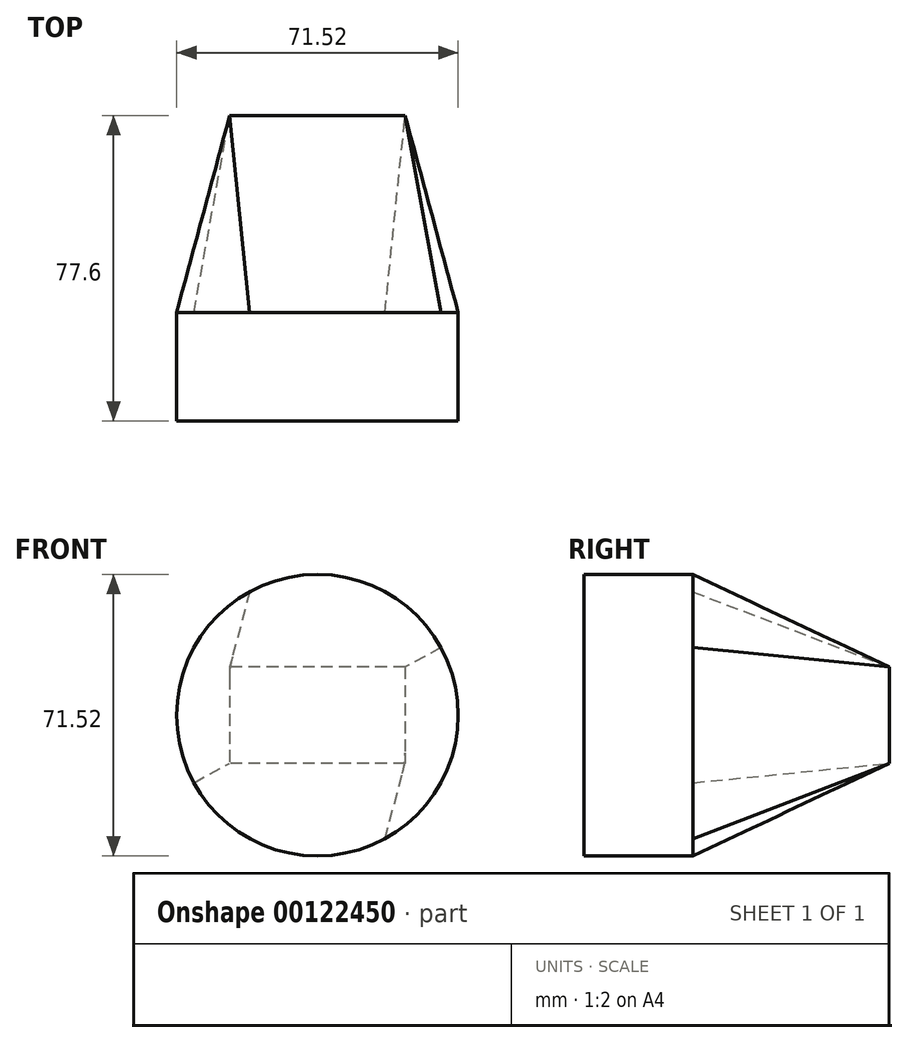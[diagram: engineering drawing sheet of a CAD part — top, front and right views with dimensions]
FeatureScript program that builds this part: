
annotation { "Feature Type Name" : "Feature", "Feature Type Description" : "" }
export const myFeature = defineFeature(function(context is Context, id is Id, definition is map)
    precondition{}
    {
        {
            var Q0;
            Q0=qCreatedBy(makeId("Front.planeOp"),FACE);
            var sketch = newSketch(context, id + "F0", { "sketchPlane" : qUnion([Q0])});
            skLineSegment(sketch, "E0.bottom", {"start": v(22.29, 12.2) * mm, "end": v(-22.29, 12.2) * mm});
            skLineSegment(sketch, "E0.top", {"start": v(22.29, -12.2) * mm, "end": v(-22.29, -12.2) * mm});
            skLineSegment(sketch, "E0.left", {"start": v(22.29, 12.2) * mm, "end": v(22.29, -12.2) * mm});
            skLineSegment(sketch, "E0.right", {"start": v(-22.29, 12.2) * mm, "end": v(-22.29, -12.2) * mm});
            skPoint(sketch, "E0.middle", {"position": v(0, 0) * mm});
            skSolve(sketch);
        }
        {
            var Q0;
            Q0=qCreatedBy(makeId("Front.planeOp"),FACE);
            cPlane(context, id + "F1", {"entities" : qUnion([Q0]), "cplaneType" : CPlaneType.OFFSET, "offset" : 50 * mm, "width" : 150 * mm, "height" : 150 * mm});
        }
        {
            var Q0;
            Q0=qCreatedBy(id+"F1.planeOp",FACE);
            var sketch = newSketch(context, id + "F2", { "sketchPlane" : qUnion([Q0])});
            skCircle(sketch, "E1", {"center": v(0, 0) * mm, "radius": 35.76 * mm});
            skSolve(sketch);
        }
        {
            var Q0;
            Q0=makeQuery(id+"F2.imprint","IMPRINT",FACE,{"disambiguationData":[TD([[makeQuery(id+"F2.imprint","IMPRINT",EDGE,{"derivedFrom":sQuery(id+"F2.wireOp",EDGE,"E1")}),1.0]])]});
            extrude(context, id + "F3", {"entities" : qUnion([Q0]), "depth" : 27.6 * mm});
        }
        {
            var Q0;
            Q0=makeQuery(id+"F3.opExtrude","CAP_FACE",FACE,{"disambiguationData":[OSD([sQuery(id+"F2.wireOp",EDGE,"E1")])],"isStart":true});
            var Q1;
            Q1=makeQuery(id+"F0.imprint","IMPRINT",FACE,{"disambiguationData":[TD([[makeQuery(id+"F0.imprint","IMPRINT",EDGE,{"derivedFrom":sQuery(id+"F0.wireOp",EDGE,"E0.bottom")}),1.0]])]});
            loft(context, id + "F4", {"sheetProfilesArray" : [{ "sheetProfileEntities" : qUnion([Q0]) }, { "sheetProfileEntities" : qUnion([Q1]) }]});
        }
    });
